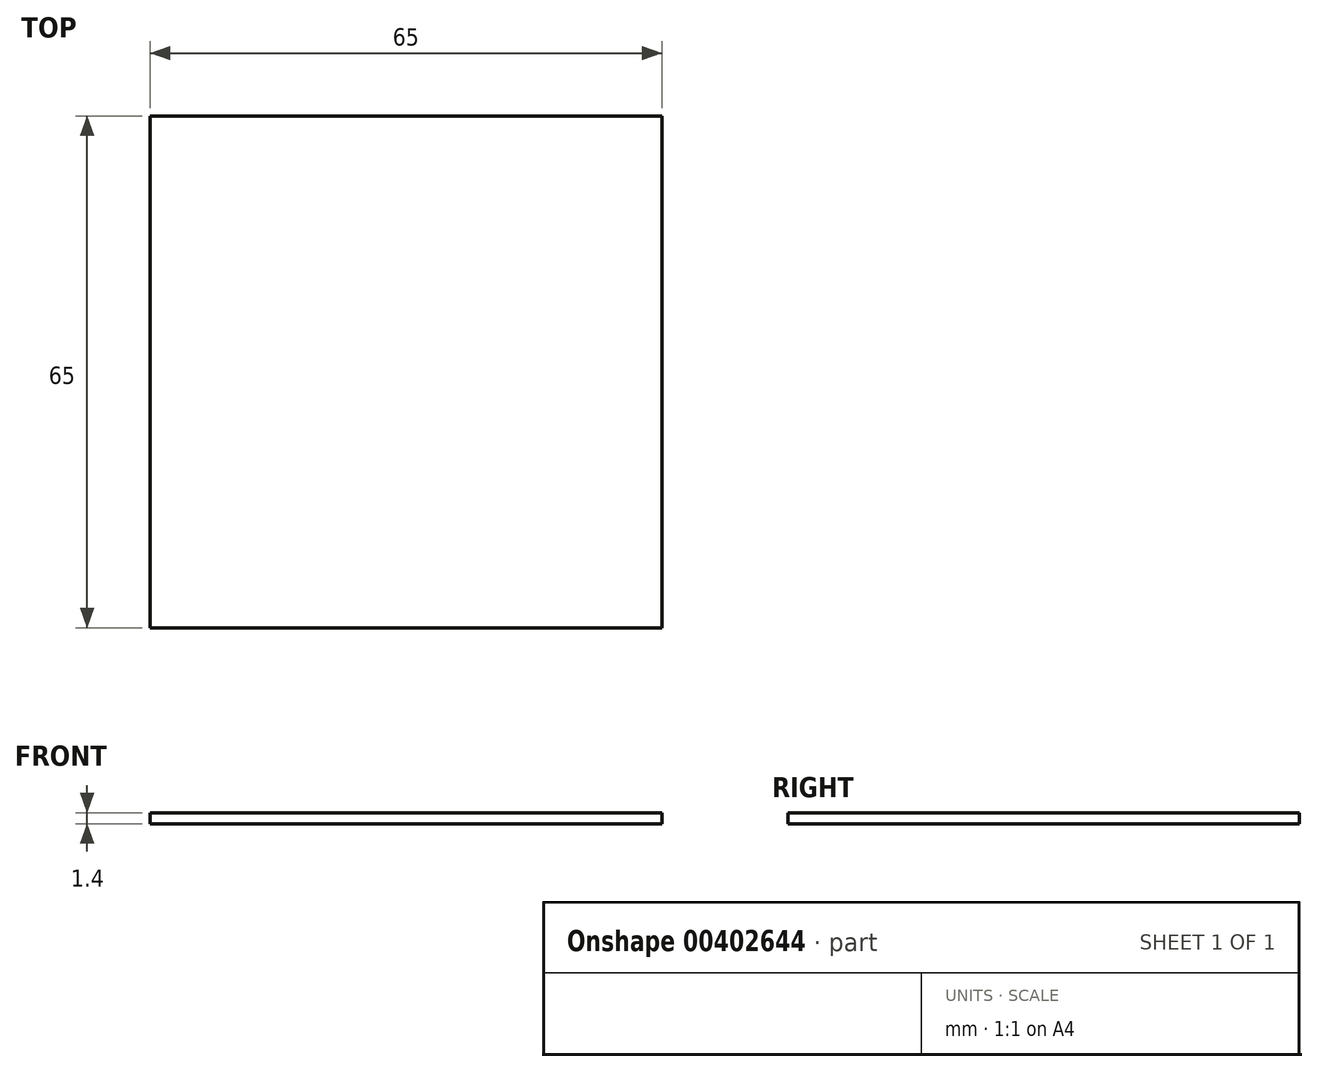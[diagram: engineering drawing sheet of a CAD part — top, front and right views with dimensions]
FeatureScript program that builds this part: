
annotation { "Feature Type Name" : "Feature", "Feature Type Description" : "" }
export const myFeature = defineFeature(function(context is Context, id is Id, definition is map)
    precondition{}
    {
        {
            var Q0;
            Q0=qCreatedBy(makeId("Top.planeOp"),FACE);
            var sketch = newSketch(context, id + "F0", { "sketchPlane" : qUnion([Q0])});
            skLineSegment(sketch, "E0.bottom", {"start": v(0, 0) * mm, "end": v(-65, 0) * mm});
            skLineSegment(sketch, "E0.top", {"start": v(0, 65) * mm, "end": v(-65, 65) * mm});
            skLineSegment(sketch, "E0.left", {"start": v(0, 0) * mm, "end": v(0, 65) * mm});
            skLineSegment(sketch, "E0.right", {"start": v(-65, 0) * mm, "end": v(-65, 65) * mm});
            skSolve(sketch);
        }
        {
            var Q0;
            Q0=makeQuery(id+"F0.imprint","IMPRINT",FACE,{"disambiguationData":[TD([[makeQuery(id+"F0.imprint","IMPRINT",EDGE,{"derivedFrom":sQuery(id+"F0.wireOp",EDGE,"E0.bottom")}),-1.0]])]});
            extrude(context, id + "F1", {"entities" : qUnion([Q0]), "depth" : 1.4 * mm});
        }
    });
